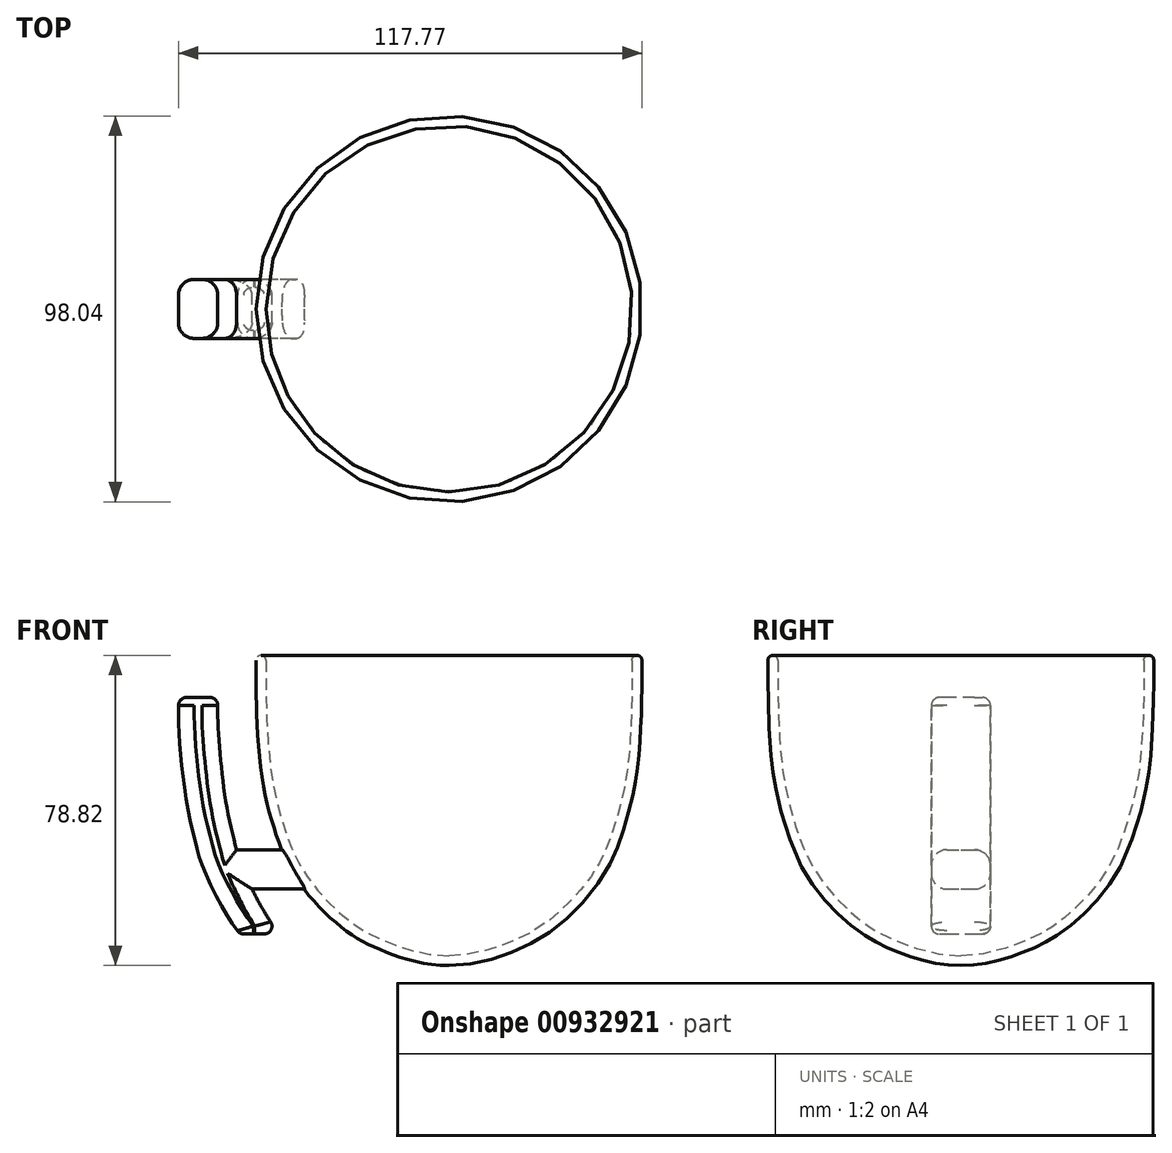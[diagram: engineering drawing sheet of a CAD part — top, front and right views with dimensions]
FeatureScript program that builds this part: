
annotation { "Feature Type Name" : "Feature", "Feature Type Description" : "" }
export const myFeature = defineFeature(function(context is Context, id is Id, definition is map)
    precondition{}
    {
        {
            var Q0;
            Q0=qCreatedBy(makeId("Front.planeOp"),FACE);
            var sketch = newSketch(context, id + "F0", { "sketchPlane" : qUnion([Q0])});
            skLineSegment(sketch, "E0", {"start": v(0, 78.82) * mm, "end": v(-49, 78.82) * mm});
            skLineSegment(sketch, "E1", {"start": v(0, 0) * mm, "end": v(0, 78.82) * mm});
            skFitSpline(sketch, "E2", {"points": [v(-49, 78.82) * mm, v(-49, 71.2) * mm, v(-47.95, 50.94) * mm, v(-44.24, 34.32) * mm, v(-38.54, 21.8) * mm, v(-27.37, 9.77) * mm, v(-17.3, 3.96) * mm, v(0, 0) * mm], "startDerivative": vector(-0.53, -120.05) * mm, "endDerivative": vector(126.32, 0) * mm});
            skSolve(sketch);
        }
        {
            var Q0;
            Q0 = qSketchRegion(id + "F0", true);
            var Q1;
            Q1=sQuery(id+"F0.wireOp",EDGE,"E1");
            revolve(context, id + "F1", {"surfaceOperationType" : NewSurfaceOperationType.NEW, "entities" : qUnion([Q0]), "axis" : qUnion([Q1]), "revolveType" : RevolveType.FULL});
        }
        {
            var Q0;
            Q0=makeQuery(id+"F1.opRevolve","SWEPT_FACE",FACE,{"disambiguationData":[OSD([sQuery(id+"F0.wireOp",EDGE,"E0")])]});
            shell(context, id + "F2", {"entities" : qUnion([Q0]), "thickness" : 2.5 * mm});
        }
        {
            var Q0;
            Q0=makeQuery(id+"F1.opRevolve","SWEPT_EDGE",EDGE,{"disambiguationData":[OSD([sQuery(id+"F0.wireOp",EDGE,"E0"),sQuery(id+"F0.wireOp",EDGE,"E2")])]});
            var Q1;
            Q1=makeQuery(id+"F2.opShell","OFFSET_EDGE",EDGE,{"disambiguationData":[OSD([sQuery(id+"F0.wireOp",EDGE,"E0"),sQuery(id+"F0.wireOp",EDGE,"E2")])]});
            fillet(context, id + "F3", {"entities" : qUnion([Q0, Q1]), "radius" : 1.25 * mm, "tangentPropagation" : true, "allowEdgeOverflow" : false});
        }
        {
            var Q0;
            Q0=qCreatedBy(makeId("Front.planeOp"),FACE);
            var sketch = newSketch(context, id + "F4", { "sketchPlane" : qUnion([Q0])});
            skLineSegment(sketch, "E3", {"start": v(-41.77, 30.38) * mm, "end": v(-53.43, 30.38) * mm});
            skLineSegment(sketch, "E4", {"start": v(-49.23, 20.12) * mm, "end": v(-36.53, 20.12) * mm});
            skLineSegment(sketch, "E5", {"start": v(-36.53, 20.12) * mm, "end": v(-41.77, 30.38) * mm});
            skFitSpline(sketch, "E6", {"points": [v(-42.03, 8) * mm, v(-47.44, 16.94) * mm, v(-49.23, 20.12) * mm, v(-51.33, 24.44) * mm, v(-53.43, 30.38) * mm, v(-55.23, 38.72) * mm, v(-56.67, 49.18) * mm, v(-57.32, 61.86) * mm, v(-57.58, 68.13) * mm, v(-57.6, 68.09) * mm], "startDerivative": vector(-47.1, 69.03) * mm, "endDerivative": vector(-6.03, -13.35) * mm});
            skLineSegment(sketch, "E7", {"start": v(-57.58, 68.13) * mm, "end": v(-69.83, 68.13) * mm});
            skFitSpline(sketch, "E8", {"points": [v(-69.83, 68.13) * mm, v(-69.83, 61.07) * mm, v(-69.06, 51.29) * mm, v(-67.63, 40.46) * mm, v(-65.54, 31.18) * mm, v(-63.64, 25) * mm, v(-58.64, 14.66) * mm, v(-54.3, 8) * mm], "startDerivative": vector(-1.12, -53.42) * mm, "endDerivative": vector(31.44, -44.67) * mm});
            skLineSegment(sketch, "E9", {"start": v(-54.3, 8) * mm, "end": v(-42.03, 8) * mm});
            skSolve(sketch);
        }
        {
            var Q0;
            Q0=qCreatedBy(makeId("Right.planeOp"),FACE);
            cPlane(context, id + "F5", {"entities" : qUnion([Q0]), "cplaneType" : CPlaneType.OFFSET, "offset" : 55 * mm, "oppositeDirection" : true, "width" : 150 * mm, "height" : 150 * mm});
        }
        {
            var Q0;
            Q0=qCreatedBy(id+"F5.planeOp",FACE);
            var sketch = newSketch(context, id + "F6", { "sketchPlane" : qUnion([Q0])});
            skLineSegment(sketch, "E10.bottom", {"start": v(7.5, 29.44) * mm, "end": v(-7.5, 29.44) * mm});
            skLineSegment(sketch, "E10.top", {"start": v(7.5, 19.44) * mm, "end": v(-7.5, 19.44) * mm});
            skLineSegment(sketch, "E10.left", {"start": v(7.5, 29.44) * mm, "end": v(7.5, 19.44) * mm});
            skLineSegment(sketch, "E10.right", {"start": v(-7.5, 29.44) * mm, "end": v(-7.5, 19.44) * mm});
            skPoint(sketch, "E10.middle", {"position": v(0, 24.44) * mm});
            skSolve(sketch);
        }
        {
            var Q0;
            Q0 = qSketchRegion(id + "F6", true);
            extrude(context, id + "F7", {"entities" : qUnion([Q0]), "operationType" : NewBodyOperationType.ADD, "endBound" : BoundingType.UP_TO_NEXT, "depth" : 25 * mm, "offsetDistance" : 25 * mm});
        }
        {
            var Q0;
            Q0=qCreatedBy(makeId("Top.planeOp"),FACE);
            cPlane(context, id + "F8", {"entities" : qUnion([Q0]), "cplaneType" : CPlaneType.OFFSET, "offset" : 8 * mm, "width" : 150 * mm, "height" : 150 * mm});
        }
        {
            var Q0;
            Q0=qCreatedBy(id+"F8.planeOp",FACE);
            var sketch = newSketch(context, id + "F9", { "sketchPlane" : qUnion([Q0])});
            skLineSegment(sketch, "E11.bottom", {"start": v(-43.17, 7.5) * mm, "end": v(-53.17, 7.5) * mm});
            skLineSegment(sketch, "E11.top", {"start": v(-43.17, -7.5) * mm, "end": v(-53.17, -7.5) * mm});
            skLineSegment(sketch, "E11.left", {"start": v(-43.17, 7.5) * mm, "end": v(-43.17, -7.5) * mm});
            skLineSegment(sketch, "E11.right", {"start": v(-53.17, 7.5) * mm, "end": v(-53.17, -7.5) * mm});
            skPoint(sketch, "E11.middle", {"position": v(-48.17, 0) * mm});
            skSolve(sketch);
        }
        {
            var Q0;
            Q0=makeQuery(id+"F9.imprint","IMPRINT",FACE,{"disambiguationData":[TD([[makeQuery(id+"F9.imprint","IMPRINT",EDGE,{"derivedFrom":sQuery(id+"F9.wireOp",EDGE,"E11.bottom")}),1.0]])]});
            var Q1;
            Q1=sQuery(id+"F4.wireOp",EDGE,"E8");
            sweep(context, id + "F10", {"operationType" : NewBodyOperationType.ADD, "profiles" : qUnion([Q0]), "path" : qUnion([Q1]), "keepProfileOrientation" : true});
        }
        {
            var Q0;
            {var subQ0=sQuery(id+"F9.wireOp",EDGE,"E11.top");var subQ1=sQuery(id+"F4.wireOp",EDGE,"E8");var subQ2=sQuery(id+"F9.wireOp",EDGE,"E11.left");Q0=makeQuery(id+"F10.boolean.opBoolean","SPLIT",EDGE,{"disambiguationData":[TD([makeQuery(id+"F7.opExtrude","SWEPT_FACE",FACE,{"disambiguationData":[OSD([sQuery(id+"F6.wireOp",EDGE,"E10.bottom")])]})])],"derivedFrom":makeQuery(id+"F10.opSweep","SWEPT_EDGE",EDGE,{"disambiguationData":[OSD([subQ1,subQ0,subQ2])]})});}
            var Q1;
            {var subQ0=sQuery(id+"F9.wireOp",EDGE,"E11.bottom");var subQ1=sQuery(id+"F4.wireOp",EDGE,"E8");var subQ2=sQuery(id+"F9.wireOp",EDGE,"E11.left");Q1=makeQuery(id+"F10.boolean.opBoolean","SPLIT",EDGE,{"disambiguationData":[TD([makeQuery(id+"F7.opExtrude","SWEPT_FACE",FACE,{"disambiguationData":[OSD([sQuery(id+"F6.wireOp",EDGE,"E10.bottom")])]})])],"derivedFrom":makeQuery(id+"F10.opSweep","SWEPT_EDGE",EDGE,{"disambiguationData":[OSD([subQ1,subQ0,subQ2])]})});}
            var Q2;
            {var subQ0=sQuery(id+"F9.wireOp",EDGE,"E11.top");var subQ1=sQuery(id+"F4.wireOp",EDGE,"E8");var subQ2=sQuery(id+"F9.wireOp",EDGE,"E11.left");Q2=makeQuery(id+"F10.boolean.opBoolean","SPLIT",EDGE,{"disambiguationData":[TD([makeQuery(id+"F7.opExtrude","SWEPT_FACE",FACE,{"disambiguationData":[OSD([sQuery(id+"F6.wireOp",EDGE,"E10.top")])]})])],"derivedFrom":makeQuery(id+"F10.opSweep","SWEPT_EDGE",EDGE,{"disambiguationData":[OSD([subQ1,subQ0,subQ2])]})});}
            var Q3;
            {var subQ0=sQuery(id+"F9.wireOp",EDGE,"E11.left");var subQ1=sQuery(id+"F9.wireOp",EDGE,"E11.bottom");var subQ2=sQuery(id+"F4.wireOp",EDGE,"E8");Q3=makeQuery(id+"F10.boolean.opBoolean","SPLIT",EDGE,{"disambiguationData":[TD([makeQuery(id+"F7.opExtrude","SWEPT_FACE",FACE,{"disambiguationData":[OSD([sQuery(id+"F6.wireOp",EDGE,"E10.top")])]})])],"derivedFrom":makeQuery(id+"F10.opSweep","SWEPT_EDGE",EDGE,{"disambiguationData":[OSD([subQ2,subQ1,subQ0])]})});}
            var Q4;
            Q4=makeQuery(id+"F10.opSweep","SWEPT_EDGE",EDGE,{"disambiguationData":[OSD([sQuery(id+"F4.wireOp",EDGE,"E8"),sQuery(id+"F9.wireOp",EDGE,"E11.top"),sQuery(id+"F9.wireOp",EDGE,"E11.right")])]});
            var Q5;
            Q5=makeQuery(id+"F10.opSweep","SWEPT_EDGE",EDGE,{"disambiguationData":[OSD([sQuery(id+"F4.wireOp",EDGE,"E8"),sQuery(id+"F9.wireOp",EDGE,"E11.bottom"),sQuery(id+"F9.wireOp",EDGE,"E11.right")])]});
            var Q6;
            Q6=makeQuery(id+"F7.opExtrude","SWEPT_EDGE",EDGE,{"disambiguationData":[OSD([sQuery(id+"F6.wireOp",EDGE,"E10.bottom"),sQuery(id+"F6.wireOp",EDGE,"E10.right")])]});
            var Q7;
            Q7=makeQuery(id+"F7.opExtrude","SWEPT_EDGE",EDGE,{"disambiguationData":[OSD([sQuery(id+"F6.wireOp",EDGE,"E10.top"),sQuery(id+"F6.wireOp",EDGE,"E10.right")])]});
            var Q8;
            Q8=makeQuery(id+"F7.opExtrude","SWEPT_EDGE",EDGE,{"disambiguationData":[OSD([sQuery(id+"F6.wireOp",EDGE,"E10.top"),sQuery(id+"F6.wireOp",EDGE,"E10.left")])]});
            var Q9;
            Q9=makeQuery(id+"F7.opExtrude","SWEPT_EDGE",EDGE,{"disambiguationData":[OSD([sQuery(id+"F6.wireOp",EDGE,"E10.bottom"),sQuery(id+"F6.wireOp",EDGE,"E10.left")])]});
            fillet(context, id + "F11", {"entities" : qUnion([Q0, Q1, Q2, Q3, Q4, Q5, Q6, Q7, Q8, Q9]), "radius" : 4 * mm, "tangentPropagation" : true, "allowEdgeOverflow" : false});
        }
        {
            var Q0;
            Q0=makeQuery(id+"F10.opSweep","CAP_FACE",FACE,{"disambiguationData":[OSD([sQuery(id+"F4.wireOp",VERTEX,"E8.start"),sQuery(id+"F9.wireOp",EDGE,"E11.bottom"),sQuery(id+"F9.wireOp",EDGE,"E11.top"),sQuery(id+"F9.wireOp",EDGE,"E11.left"),sQuery(id+"F9.wireOp",EDGE,"E11.right")])],"isStart":false});
            var Q1;
            Q1=makeQuery(id+"F10.opSweep","CAP_FACE",FACE,{"disambiguationData":[OSD([sQuery(id+"F4.wireOp",VERTEX,"E8.end"),sQuery(id+"F9.wireOp",EDGE,"E11.bottom"),sQuery(id+"F9.wireOp",EDGE,"E11.top"),sQuery(id+"F9.wireOp",EDGE,"E11.left"),sQuery(id+"F9.wireOp",EDGE,"E11.right")])],"isStart":true});
            fillet(context, id + "F12", {"entities" : qUnion([Q0, Q1]), "radius" : 2 * mm, "tangentPropagation" : true, "allowEdgeOverflow" : false});
        }
    });
